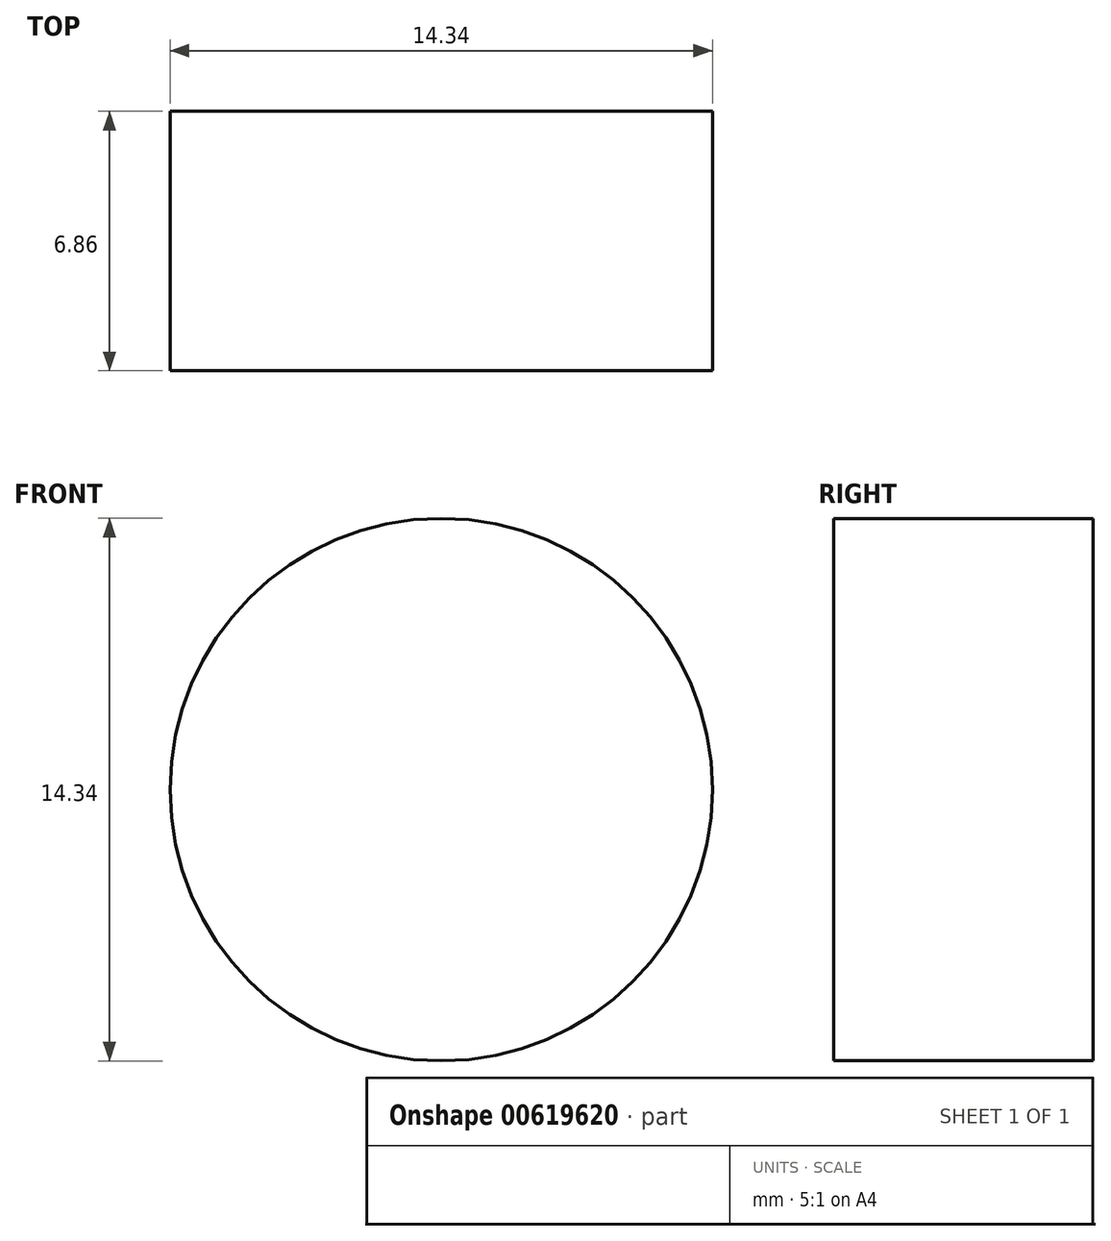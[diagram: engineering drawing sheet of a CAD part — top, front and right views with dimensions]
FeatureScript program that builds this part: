
annotation { "Feature Type Name" : "Feature", "Feature Type Description" : "" }
export const myFeature = defineFeature(function(context is Context, id is Id, definition is map)
    precondition{}
    {
        {
            var Q0;
            Q0=qCreatedBy(makeId("Front.planeOp"),FACE);
            var sketch = newSketch(context, id + "F0", { "sketchPlane" : qUnion([Q0])});
            skCircle(sketch, "E0", {"center": v(0, 0) * mm, "radius": 7.17 * mm});
            skSolve(sketch);
        }
        {
            var Q0;
            Q0=makeQuery(id+"F0.imprint","IMPRINT",FACE,{"disambiguationData":[TD([[makeQuery(id+"F0.imprint","IMPRINT",EDGE,{"derivedFrom":sQuery(id+"F0.wireOp",EDGE,"E0")}),1.0]])]});
            extrude(context, id + "F1", {"entities" : qUnion([Q0]), "depth" : 6.86 * mm, "offsetDistance" : 25.4 * mm});
        }
    });
